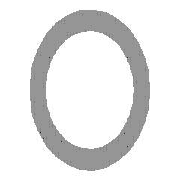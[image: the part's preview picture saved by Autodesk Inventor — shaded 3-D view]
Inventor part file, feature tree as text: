
AUTODESK INVENTOR PART (.ipt)
format: ipt  version: 2021 (Build 250183000, 183)  size: 404,480 bytes
history: native  units: mm (DEFAULTED — no unit token found)
features: other x7, plane x3, sketch x3, sweep x1, split x1
ambient origin geometry x8: Origin, YZ Plane, XZ Plane, XY Plane, X Axis, Y Axis, Z Axis, Center Point
bodies: Solid1 (feature_tree)
feature tree (15):
  parser-record x1  (decoder bookkeeping rows leaked as tree rows — omitted from the tree; the rows remain in map.json)
  other  "Driven Length"
  other  "Plano inicial"
  other  "Plano final"
  other  "Trayectoria de barrido"
  plane  "Plano de trabajo de orientación"
  sweep  "Cuerpo"
  plane  "Plano de trabajo9"
  split  "Dividir5"
  sketch  "Sketch3"  dims[d0=26.67mm d1=3.9116mm]
  plane  "Work Plane3"
  sketch  "Sketch4"  dims[d4=-0.0mm]
  sketch  "Boceto9"  dims[d5=1126.193571mm d6=90.0deg d7=1126.193571mm d8=0.0mm d9=0.0mm d26=0.0mm d27=90.0deg d28=0.0mm d29=90.0deg]
  other  "Sup5"
  other  "SuperficieSolevación5"
